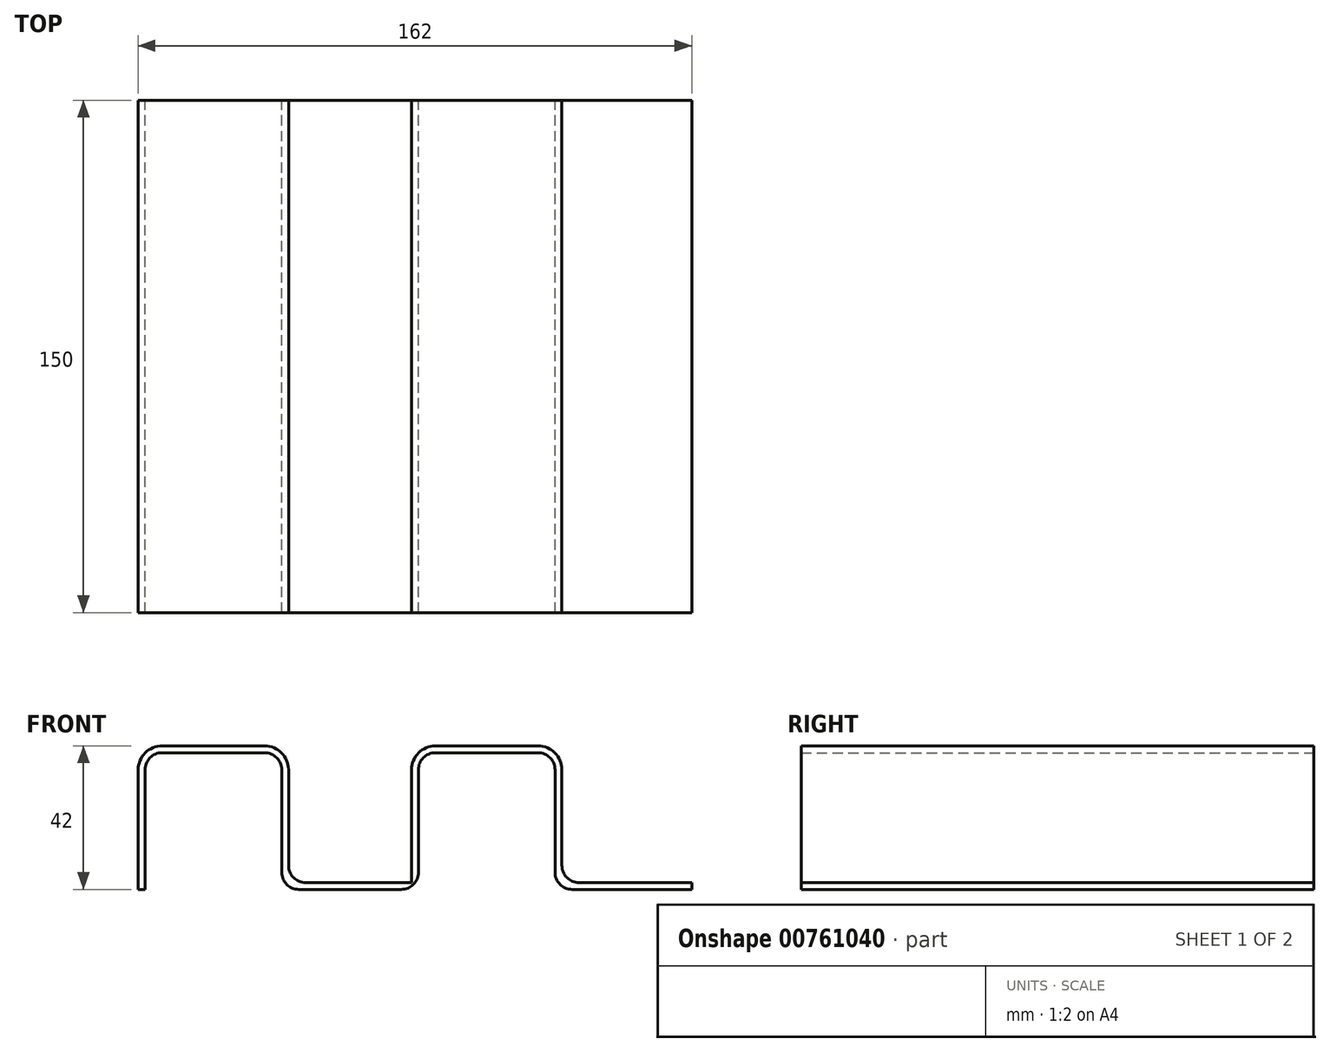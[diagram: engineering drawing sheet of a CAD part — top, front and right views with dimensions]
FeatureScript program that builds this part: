
annotation { "Feature Type Name" : "Feature", "Feature Type Description" : "" }
export const myFeature = defineFeature(function(context is Context, id is Id, definition is map)
    precondition{}
    {
        {
            var Q0;
            Q0=qCreatedBy(makeId("Front.planeOp"),FACE);
            var sketch = newSketch(context, id + "F0", { "sketchPlane" : qUnion([Q0])});
            skLineSegment(sketch, "E0.top", {"start": v(5, 40) * mm, "end": v(35, 40) * mm});
            skLineSegment(sketch, "E0.left", {"start": v(0, 0) * mm, "end": v(0, 35) * mm});
            skLineSegment(sketch, "E0.right", {"start": v(40, 5) * mm, "end": v(40, 35) * mm});
            skPoint(sketch, "E1.visualSharp", {"position": v(0, 40) * mm});
            skArc(sketch, "E1.filletArc", {"start": v(5, 40) * mm, "mid": v(1.46, 38.54) * mm, "end": v(0, 35) * mm});
            skPoint(sketch, "E2.visualSharp", {"position": v(40, 40) * mm});
            skArc(sketch, "E2.filletArc", {"start": v(40, 35) * mm, "mid": v(38.54, 38.54) * mm, "end": v(35, 40) * mm});
            skLineSegment(sketch, "E3", {"start": v(45, 0) * mm, "end": v(75, 0) * mm});
            skPoint(sketch, "E4.visualSharp", {"position": v(40, 0) * mm});
            skArc(sketch, "E4.filletArc", {"start": v(40, 5) * mm, "mid": v(41.46, 1.46) * mm, "end": v(45, 0) * mm});
            skLineSegment(sketch, "E5", {"start": v(80, 5) * mm, "end": v(80, 35) * mm});
            skLineSegment(sketch, "E6", {"start": v(85, 40) * mm, "end": v(115, 40) * mm});
            skPoint(sketch, "E7.visualSharp", {"position": v(80, 0) * mm});
            skArc(sketch, "E7.filletArc", {"start": v(75, 0) * mm, "mid": v(78.54, 1.46) * mm, "end": v(80, 5) * mm});
            skPoint(sketch, "E8.visualSharp", {"position": v(80, 40) * mm});
            skArc(sketch, "E8.filletArc", {"start": v(85, 40) * mm, "mid": v(81.46, 38.54) * mm, "end": v(80, 35) * mm});
            skLineSegment(sketch, "E9", {"start": v(120, 35) * mm, "end": v(120, 5) * mm});
            skLineSegment(sketch, "E10", {"start": v(125, 0) * mm, "end": v(160, 0) * mm});
            skPoint(sketch, "E11.visualSharp", {"position": v(120, 40) * mm});
            skArc(sketch, "E11.filletArc", {"start": v(120, 35) * mm, "mid": v(118.54, 38.54) * mm, "end": v(115, 40) * mm});
            skPoint(sketch, "E12.visualSharp", {"position": v(120, 0) * mm});
            skArc(sketch, "E12.filletArc", {"start": v(120, 5) * mm, "mid": v(121.46, 1.46) * mm, "end": v(125, 0) * mm});
            skLineSegment(sketch, "E13.0", {"start": v(-2, 0) * mm, "end": v(-2, 35) * mm});
            skArc(sketch, "E13.1", {"start": v(5, 42) * mm, "mid": v(0.05, 39.95) * mm, "end": v(-2, 35) * mm});
            skLineSegment(sketch, "E13.2", {"start": v(85, 42) * mm, "end": v(115, 42) * mm});
            skArc(sketch, "E13.3", {"start": v(122, 35) * mm, "mid": v(119.95, 39.95) * mm, "end": v(115, 42) * mm});
            skLineSegment(sketch, "E13.4", {"start": v(122, 35) * mm, "end": v(122, 2) * mm});
            skLineSegment(sketch, "E13.5", {"start": v(122, 2) * mm, "end": v(160, 2) * mm});
            skArc(sketch, "E13.6", {"start": v(85, 42) * mm, "mid": v(80.05, 39.95) * mm, "end": v(78, 35) * mm});
            skLineSegment(sketch, "E13.7", {"start": v(78, 2) * mm, "end": v(78, 35) * mm});
            skLineSegment(sketch, "E13.8", {"start": v(42, 2) * mm, "end": v(78, 2) * mm});
            skLineSegment(sketch, "E13.9", {"start": v(42, 2) * mm, "end": v(42, 35) * mm});
            skArc(sketch, "E13.10", {"start": v(42, 35) * mm, "mid": v(39.95, 39.95) * mm, "end": v(35, 42) * mm});
            skLineSegment(sketch, "E13.11", {"start": v(5, 42) * mm, "end": v(35, 42) * mm});
            skLineSegment(sketch, "E14", {"start": v(-2, 0) * mm, "end": v(0, 0) * mm});
            skLineSegment(sketch, "E15", {"start": v(160, 2) * mm, "end": v(160, 0) * mm});
            skSolve(sketch);
        }
        {
            var Q0;
            Q0=makeQuery(id+"F0.imprint","IMPRINT",FACE,{"disambiguationData":[TD([[makeQuery(id+"F0.imprint","IMPRINT",EDGE,{"derivedFrom":sQuery(id+"F0.wireOp",EDGE,"E0.top")}),1.0]])]});
            extrude(context, id + "F1", {"entities" : qUnion([Q0]), "depth" : 150 * mm, "offsetDistance" : 25 * mm});
        }
        {
            var Q0;
            Q0=makeQuery(id+"F1.opExtrude","SWEPT_EDGE",EDGE,{"disambiguationData":[OSD([sQuery(id+"F0.wireOp",EDGE,"E13.8"),sQuery(id+"F0.wireOp",EDGE,"E13.9")])]});
            var Q1;
            Q1=makeQuery(id+"F1.opExtrude","SWEPT_EDGE",EDGE,{"disambiguationData":[OSD([sQuery(id+"F0.wireOp",EDGE,"E13.4"),sQuery(id+"F0.wireOp",EDGE,"E13.5")])]});
            fillet(context, id + "F2", {"entities" : qUnion([Q0, Q1]), "radius" : 5 * mm, "tangentPropagation" : true, "allowEdgeOverflow" : false});
        }
    });
